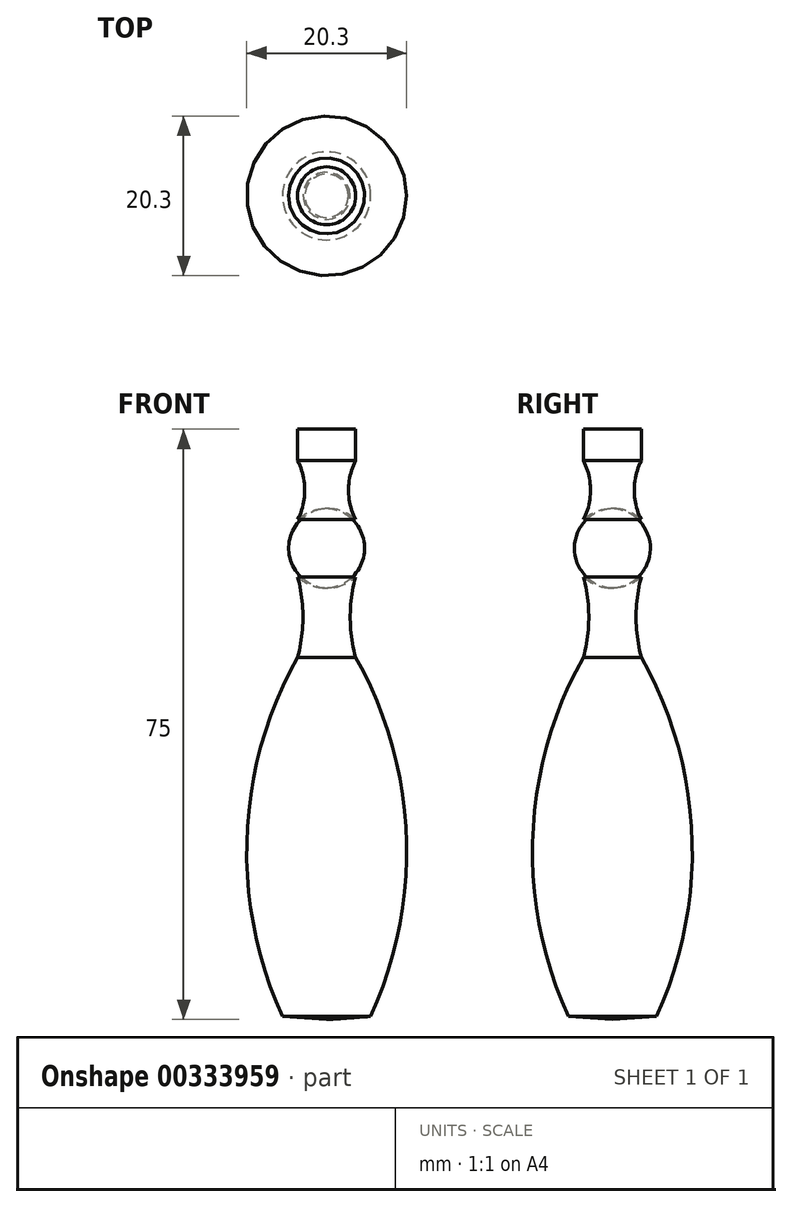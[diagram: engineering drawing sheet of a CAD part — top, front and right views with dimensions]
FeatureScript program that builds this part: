
annotation { "Feature Type Name" : "Feature", "Feature Type Description" : "" }
export const myFeature = defineFeature(function(context is Context, id is Id, definition is map)
    precondition{}
    {
        {
            var Q0;
            Q0=qCreatedBy(makeId("Front.planeOp"),FACE);
            var sketch = newSketch(context, id + "F0", { "sketchPlane" : qUnion([Q0])});
            skLineSegment(sketch, "E0", {"start": v(0, 0) * mm, "end": v(0, -75) * mm});
            skLineSegment(sketch, "E1", {"start": v(0, 0) * mm, "end": v(3.68, 0) * mm});
            skLineSegment(sketch, "E2", {"start": v(3.68, 0) * mm, "end": v(3.68, -4) * mm});
            skArc(sketch, "E3", {"start": v(3.68, -4) * mm, "mid": v(2.78, -7.74) * mm, "end": v(3.68, -11.49) * mm});
            skArc(sketch, "E4", {"start": v(3.68, -18.75) * mm, "mid": v(5.23, -15.12) * mm, "end": v(3.68, -11.49) * mm});
            skArc(sketch, "E5", {"start": v(5.6, -74.6) * mm, "mid": v(10.1, -51.55) * mm, "end": v(3.68, -28.97) * mm});
            skLineSegment(sketch, "E6", {"start": v(5.6, -74.6) * mm, "end": v(0, -75) * mm});
            skArc(sketch, "E7", {"start": v(3.68, -18.75) * mm, "mid": v(3, -23.86) * mm, "end": v(3.68, -28.97) * mm});
            skSolve(sketch);
        }
        {
            var Q0;
            Q0=makeQuery(id+"F0.imprint","IMPRINT",FACE,{"disambiguationData":[TD([[makeQuery(id+"F0.imprint","IMPRINT",EDGE,{"derivedFrom":sQuery(id+"F0.wireOp",EDGE,"E0")}),1.0]])]});
            var Q1;
            Q1=sQuery(id+"F0.wireOp",EDGE,"E0");
            revolve(context, id + "F1", {"entities" : qUnion([Q0]), "axis" : qUnion([Q1]), "revolveType" : RevolveType.FULL});
        }
    });
